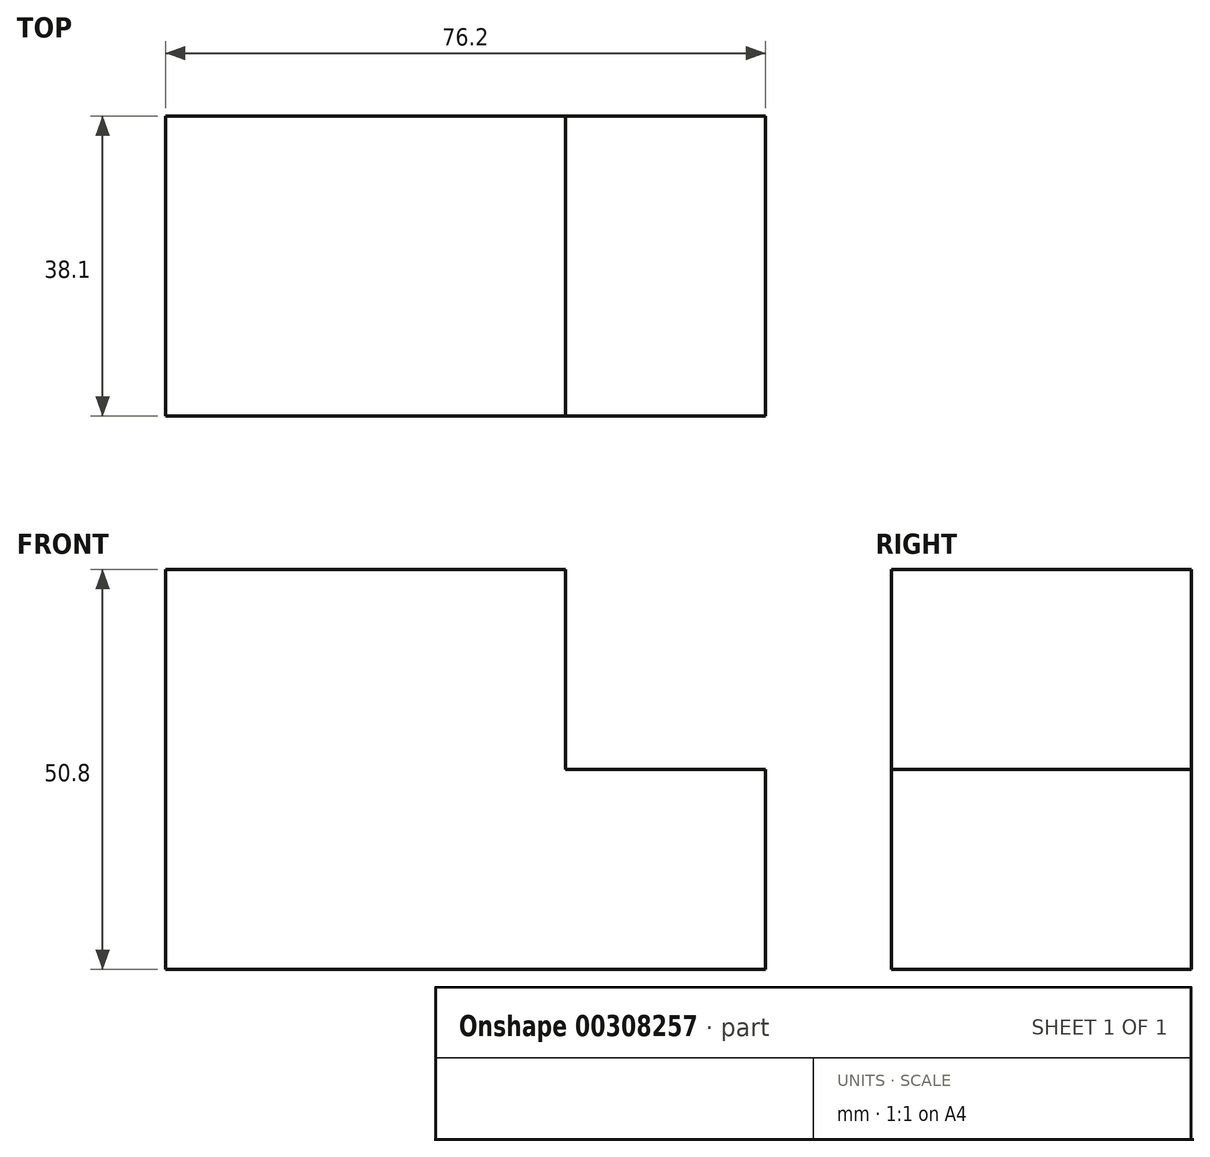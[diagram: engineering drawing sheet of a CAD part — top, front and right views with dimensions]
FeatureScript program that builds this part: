
annotation { "Feature Type Name" : "Feature", "Feature Type Description" : "" }
export const myFeature = defineFeature(function(context is Context, id is Id, definition is map)
    precondition{}
    {
        {
            var Q0;
            Q0=qCreatedBy(makeId("Front.planeOp"),FACE);
            var sketch = newSketch(context, id + "F0", { "sketchPlane" : qUnion([Q0])});
            skLineSegment(sketch, "E0", {"start": v(-49.39, -29.56) * mm, "end": v(26.81, -29.56) * mm});
            skLineSegment(sketch, "E1", {"start": v(26.81, -29.56) * mm, "end": v(26.81, -4.16) * mm});
            skLineSegment(sketch, "E2", {"start": v(26.81, -4.16) * mm, "end": v(1.41, -4.16) * mm});
            skLineSegment(sketch, "E3", {"start": v(1.41, -4.16) * mm, "end": v(1.41, 21.24) * mm});
            skLineSegment(sketch, "E4", {"start": v(1.41, 21.24) * mm, "end": v(-49.39, 21.24) * mm});
            skLineSegment(sketch, "E5", {"start": v(-49.39, 21.24) * mm, "end": v(-49.39, -29.56) * mm});
            skSolve(sketch);
        }
        {
            var Q0;
            Q0=makeQuery(id+"F0.imprint","IMPRINT",FACE,{"disambiguationData":[TD([[makeQuery(id+"F0.imprint","IMPRINT",EDGE,{"derivedFrom":sQuery(id+"F0.wireOp",EDGE,"E0")}),1.0]])]});
            extrude(context, id + "F1", {"entities" : qUnion([Q0]), "depth" : 38.1 * mm});
        }
    });
